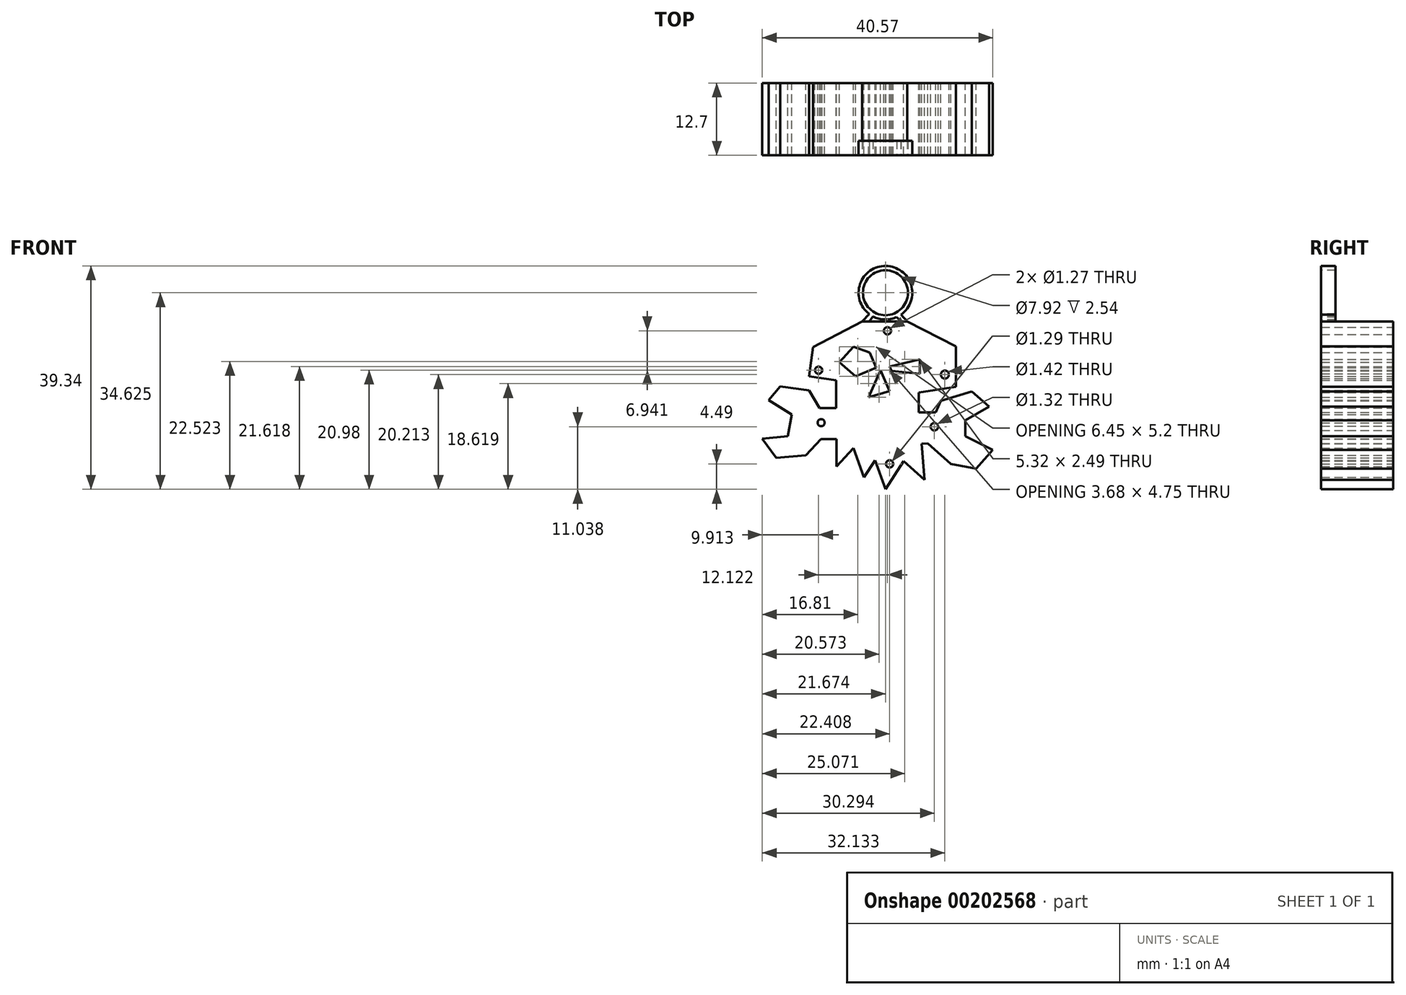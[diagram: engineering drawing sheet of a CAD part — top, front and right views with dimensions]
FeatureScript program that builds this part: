
annotation { "Feature Type Name" : "Feature", "Feature Type Description" : "" }
export const myFeature = defineFeature(function(context is Context, id is Id, definition is map)
    precondition{}
    {
        {
            var Q0;
            Q0=qCreatedBy(makeId("Front.planeOp"),FACE);
            var sketch = newSketch(context, id + "F0", { "sketchPlane" : qUnion([Q0])});
            skLineSegment(sketch, "E0", {"start": v(-63.88, 11.24) * mm, "end": v(-59.81, 8.7) * mm});
            skLineSegment(sketch, "E1", {"start": v(-59.81, 8.7) * mm, "end": v(-60.55, 4.9) * mm});
            skLineSegment(sketch, "E2", {"start": v(-60.55, 4.9) * mm, "end": v(-65.02, 4.45) * mm});
            skLineSegment(sketch, "E3", {"start": v(-65.02, 4.45) * mm, "end": v(-62.58, 1.06) * mm});
            skLineSegment(sketch, "E4", {"start": v(-62.58, 1.06) * mm, "end": v(-57.38, 1.51) * mm});
            skLineSegment(sketch, "E5", {"start": v(-57.38, 1.51) * mm, "end": v(-54.66, 4.4) * mm});
            skLineSegment(sketch, "E6", {"start": v(-54.66, 4.4) * mm, "end": v(-53.19, 4.4) * mm});
            skLineSegment(sketch, "E7", {"start": v(-53.19, 4.4) * mm, "end": v(-51.94, 4.4) * mm});
            skLineSegment(sketch, "E8", {"start": v(-51.94, 4.4) * mm, "end": v(-51.94, -0.47) * mm});
            skLineSegment(sketch, "E9", {"start": v(-51.94, -0.47) * mm, "end": v(-49, 2.81) * mm});
            skLineSegment(sketch, "E10", {"start": v(-49, 2.81) * mm, "end": v(-47.14, -2.4) * mm});
            skLineSegment(sketch, "E11", {"start": v(-47.14, -2.4) * mm, "end": v(-45.15, 0.6) * mm});
            skLineSegment(sketch, "E12", {"start": v(-45.15, 0.6) * mm, "end": v(-43.34, -4.49) * mm});
            skLineSegment(sketch, "E13", {"start": v(-43.34, -4.49) * mm, "end": v(-40.12, 0.5) * mm});
            skLineSegment(sketch, "E14", {"start": v(-40.12, 0.5) * mm, "end": v(-36.47, -2.78) * mm});
            skLineSegment(sketch, "E15", {"start": v(-36.47, -2.78) * mm, "end": v(-36.95, 3.55) * mm});
            skLineSegment(sketch, "E16", {"start": v(-36.95, 3.55) * mm, "end": v(-35.88, 3.63) * mm});
            skLineSegment(sketch, "E17", {"start": v(-35.88, 3.63) * mm, "end": v(-31.84, 0) * mm});
            skLineSegment(sketch, "E18", {"start": v(-31.84, 0) * mm, "end": v(-27.39, -0.8) * mm});
            skLineSegment(sketch, "E19", {"start": v(-27.39, -0.8) * mm, "end": v(-24.45, 2.47) * mm});
            skLineSegment(sketch, "E20", {"start": v(-24.45, 2.47) * mm, "end": v(-29.31, 4.9) * mm});
            skLineSegment(sketch, "E21", {"start": v(-29.31, 4.9) * mm, "end": v(-29.31, 7.68) * mm});
            skLineSegment(sketch, "E22", {"start": v(-29.31, 7.68) * mm, "end": v(-25.12, 10.06) * mm});
            skLineSegment(sketch, "E23", {"start": v(-25.12, 10.06) * mm, "end": v(-28.16, 12.78) * mm});
            skLineSegment(sketch, "E24", {"start": v(-28.16, 12.78) * mm, "end": v(-33.61, 11.13) * mm});
            skLineSegment(sketch, "E25", {"start": v(-33.61, 11.13) * mm, "end": v(-34.52, 9.1) * mm});
            skLineSegment(sketch, "E26", {"start": v(-34.52, 9.1) * mm, "end": v(-37.46, 9.1) * mm});
            skLineSegment(sketch, "E27", {"start": v(-37.46, 9.1) * mm, "end": v(-37.46, 12.54) * mm});
            skLineSegment(sketch, "E28", {"start": v(-37.46, 12.54) * mm, "end": v(-30.95, 13.56) * mm});
            skLineSegment(sketch, "E29", {"start": v(-30.95, 13.56) * mm, "end": v(-30.95, 20.7) * mm});
            skLineSegment(sketch, "E30", {"start": v(-30.95, 20.7) * mm, "end": v(-39.5, 25.05) * mm});
            skLineSegment(sketch, "E31", {"start": v(-39.5, 25.05) * mm, "end": v(-47.47, 25.05) * mm});
            skLineSegment(sketch, "E32", {"start": v(-47.47, 25.05) * mm, "end": v(-56.08, 20.58) * mm});
            skLineSegment(sketch, "E33", {"start": v(-56.08, 20.58) * mm, "end": v(-56.81, 15.43) * mm});
            skLineSegment(sketch, "E34", {"start": v(-56.81, 15.43) * mm, "end": v(-52.02, 14.75) * mm});
            skLineSegment(sketch, "E35", {"start": v(-52.02, 14.75) * mm, "end": v(-52.02, 9.83) * mm});
            skLineSegment(sketch, "E36", {"start": v(-52.02, 9.83) * mm, "end": v(-54.94, 9.83) * mm});
            skLineSegment(sketch, "E37", {"start": v(-54.94, 9.83) * mm, "end": v(-56.81, 12.94) * mm});
            skLineSegment(sketch, "E38", {"start": v(-56.81, 12.94) * mm, "end": v(-61.85, 13.62) * mm});
            skLineSegment(sketch, "E39", {"start": v(-61.85, 13.62) * mm, "end": v(-63.88, 11.24) * mm});
            skLineSegment(sketch, "E40", {"start": v(-51.44, 17.92) * mm, "end": v(-49, 20.63) * mm});
            skLineSegment(sketch, "E41", {"start": v(-49, 20.63) * mm, "end": v(-46.12, 19.62) * mm});
            skLineSegment(sketch, "E42", {"start": v(-46.12, 19.62) * mm, "end": v(-44.98, 16.96) * mm});
            skLineSegment(sketch, "E43", {"start": v(-44.98, 16.96) * mm, "end": v(-48.58, 15.43) * mm});
            skLineSegment(sketch, "E44", {"start": v(-48.58, 15.43) * mm, "end": v(-51.44, 17.92) * mm});
            skLineSegment(sketch, "E45", {"start": v(-42.6, 17.13) * mm, "end": v(-37.29, 18.37) * mm});
            skLineSegment(sketch, "E46", {"start": v(-37.29, 18.37) * mm, "end": v(-37.29, 15.88) * mm});
            skLineSegment(sketch, "E47", {"start": v(-37.29, 15.88) * mm, "end": v(-42.21, 16.4) * mm});
            skLineSegment(sketch, "E48", {"start": v(-42.21, 16.4) * mm, "end": v(-42.6, 17.13) * mm});
            skLineSegment(sketch, "E49", {"start": v(-46.29, 11.75) * mm, "end": v(-44.2, 16.5) * mm});
            skLineSegment(sketch, "E50", {"start": v(-44.2, 16.5) * mm, "end": v(-42.6, 12.78) * mm});
            skLineSegment(sketch, "E51", {"start": v(-42.6, 12.78) * mm, "end": v(-46.29, 11.75) * mm});
            skLineSegment(sketch, "E52", {"start": v(-53.19, 9.83) * mm, "end": v(-53.19, 4.4) * mm});
            skLineSegment(sketch, "E53", {"start": v(-35.99, 9.1) * mm, "end": v(-35.88, 3.63) * mm});
            skCircle(sketch, "E54", {"center": v(-42.99, 23.43) * mm, "radius": 0.63 * mm});
            skCircle(sketch, "E55", {"center": v(-32.89, 15.72) * mm, "radius": 0.7 * mm});
            skCircle(sketch, "E56", {"center": v(-34.73, 6.55) * mm, "radius": 0.66 * mm});
            skCircle(sketch, "E57", {"center": v(-42.61, 0) * mm, "radius": 0.64 * mm});
            skCircle(sketch, "E58", {"center": v(-54.66, 7.26) * mm, "radius": 0.63 * mm});
            skCircle(sketch, "E59", {"center": v(-55.1, 16.5) * mm, "radius": 0.63 * mm});
            skSolve(sketch);
        }
        {
            var Q0;
            Q0=makeQuery(id+"F0.imprint","IMPRINT",FACE,{"disambiguationData":[TD([[makeQuery(id+"F0.imprint","IMPRINT",EDGE,{"derivedFrom":sQuery(id+"F0.wireOp",EDGE,"E0")}),1.0]])]});
            var Q1;
            Q1=makeQuery(id+"F0.imprint","IMPRINT",FACE,{"disambiguationData":[TD([[makeQuery(id+"F0.imprint","IMPRINT",EDGE,{"derivedFrom":sQuery(id+"F0.wireOp",EDGE,"E17")}),1.0]])]});
            var Q2;
            Q2=makeQuery(id+"F0.imprint","IMPRINT",FACE,{"disambiguationData":[TD([[makeQuery(id+"F0.imprint","IMPRINT",EDGE,{"derivedFrom":sQuery(id+"F0.wireOp",EDGE,"E7")}),1.0]])]});
            extrude(context, id + "F1", {"entities" : qUnion([Q0, Q1, Q2]), "depth" : 12.7 * mm});
        }
        {
            var Q0;
            Q0=sQuery(id+"F0.wireOp",EDGE,"E59");
            var Q1;
            Q1=sQuery(id+"F0.wireOp",EDGE,"E54");
            var Q2;
            Q2=sQuery(id+"F0.wireOp",EDGE,"E55");
            var Q3;
            Q3=sQuery(id+"F0.wireOp",EDGE,"E56");
            var Q4;
            Q4=sQuery(id+"F0.wireOp",EDGE,"E57");
            var Q5;
            Q5=sQuery(id+"F0.wireOp",EDGE,"E58");
            extrude(context, id + "F2", {"bodyType" : ToolBodyType.SURFACE, "surfaceEntities" : qUnion([Q0, Q1, Q2, Q3, Q4, Q5]), "depth" : 13.46 * mm});
        }
        {
            var Q0;
            Q0=makeQuery(id+"F1.opExtrude","CAP_FACE",FACE,{"disambiguationData":[OSD([sQuery(id+"F0.wireOp",EDGE,"E0"),sQuery(id+"F0.wireOp",EDGE,"E1"),sQuery(id+"F0.wireOp",EDGE,"E2"),sQuery(id+"F0.wireOp",EDGE,"E3"),sQuery(id+"F0.wireOp",EDGE,"E4"),sQuery(id+"F0.wireOp",EDGE,"E5"),sQuery(id+"F0.wireOp",EDGE,"E6"),sQuery(id+"F0.wireOp",EDGE,"E7"),sQuery(id+"F0.wireOp",EDGE,"E8"),sQuery(id+"F0.wireOp",EDGE,"E9"),sQuery(id+"F0.wireOp",EDGE,"E10"),sQuery(id+"F0.wireOp",EDGE,"E11"),sQuery(id+"F0.wireOp",EDGE,"E12"),sQuery(id+"F0.wireOp",EDGE,"E13"),sQuery(id+"F0.wireOp",EDGE,"E14"),sQuery(id+"F0.wireOp",EDGE,"E15"),sQuery(id+"F0.wireOp",EDGE,"E16"),sQuery(id+"F0.wireOp",EDGE,"E17"),sQuery(id+"F0.wireOp",EDGE,"E18"),sQuery(id+"F0.wireOp",EDGE,"E19"),sQuery(id+"F0.wireOp",EDGE,"E20"),sQuery(id+"F0.wireOp",EDGE,"E21"),sQuery(id+"F0.wireOp",EDGE,"E22"),sQuery(id+"F0.wireOp",EDGE,"E23"),sQuery(id+"F0.wireOp",EDGE,"E24"),sQuery(id+"F0.wireOp",EDGE,"E25"),sQuery(id+"F0.wireOp",EDGE,"E26"),sQuery(id+"F0.wireOp",EDGE,"E27"),sQuery(id+"F0.wireOp",EDGE,"E28"),sQuery(id+"F0.wireOp",EDGE,"E29"),sQuery(id+"F0.wireOp",EDGE,"E30"),sQuery(id+"F0.wireOp",EDGE,"E31"),sQuery(id+"F0.wireOp",EDGE,"E32"),sQuery(id+"F0.wireOp",EDGE,"E33"),sQuery(id+"F0.wireOp",EDGE,"E34"),sQuery(id+"F0.wireOp",EDGE,"E35"),sQuery(id+"F0.wireOp",EDGE,"E36"),sQuery(id+"F0.wireOp",EDGE,"E37"),sQuery(id+"F0.wireOp",EDGE,"E38"),sQuery(id+"F0.wireOp",EDGE,"E39"),sQuery(id+"F0.wireOp",EDGE,"E40"),sQuery(id+"F0.wireOp",EDGE,"E41"),sQuery(id+"F0.wireOp",EDGE,"E42"),sQuery(id+"F0.wireOp",EDGE,"E43"),sQuery(id+"F0.wireOp",EDGE,"E44"),sQuery(id+"F0.wireOp",EDGE,"E45"),sQuery(id+"F0.wireOp",EDGE,"E46"),sQuery(id+"F0.wireOp",EDGE,"E47"),sQuery(id+"F0.wireOp",EDGE,"E48"),sQuery(id+"F0.wireOp",EDGE,"E49"),sQuery(id+"F0.wireOp",EDGE,"E50"),sQuery(id+"F0.wireOp",EDGE,"E51"),sQuery(id+"F0.wireOp",EDGE,"E54"),sQuery(id+"F0.wireOp",EDGE,"E55"),sQuery(id+"F0.wireOp",EDGE,"E56"),sQuery(id+"F0.wireOp",EDGE,"E57"),sQuery(id+"F0.wireOp",EDGE,"E58"),sQuery(id+"F0.wireOp",EDGE,"E59")])],"isStart":false});
            var sketch = newSketch(context, id + "F3", { "sketchPlane" : qUnion([Q0])});
            skLineSegment(sketch, "E60", {"start": v(-47.47, 25.05) * mm, "end": v(-46.21, 26.38) * mm});
            skLineSegment(sketch, "E61", {"start": v(-39.5, 25.05) * mm, "end": v(-40.67, 26.38) * mm});
            skLineSegment(sketch, "E62", {"start": v(-40.67, 25.05) * mm, "end": v(-41.85, 26.38) * mm});
            skLineSegment(sketch, "E63", {"start": v(-46.21, 25.05) * mm, "end": v(-45.18, 26.38) * mm});
            skCircle(sketch, "E64", {"center": v(-43.35, 30.13) * mm, "radius": 4.72 * mm});
            skCircle(sketch, "E65", {"center": v(-43.35, 30.13) * mm, "radius": 3.96 * mm});
            skSolve(sketch);
        }
        {
            var Q0;
            Q0 = qSketchRegion(id + "F3", true);
            var Q1;
            {var subQ0=sQuery(id+"F3.wireOp",EDGE,"E60");Q1=makeQuery(id+"F3.imprint","IMPRINT",FACE,{"disambiguationData":[TD([[makeQuery(id+"F3.imprint","IMPRINT",EDGE,{"derivedFrom":subQ0}),-1.0]])]});}
            var Q2;
            {var subQ1=makeQuery(id+"F1.opExtrude","CAP_EDGE",EDGE,{"disambiguationData":[OSD([sQuery(id+"F0.wireOp",EDGE,"E31")])],"isStart":false});var subQ5=sQuery(id+"F3.wireOp",EDGE,"E62");var subQ6=makeQuery(id+"F3.imprint","INTERSECT",VERTEX,{"derivedFrom":[subQ1,subQ5]});Q2=makeQuery(id+"F3.imprint","IMPRINT",FACE,{"disambiguationData":[TD([[makeQuery(id+"F3.imprint","IMPRINT",EDGE,{"disambiguationData":[TD([[subQ6,-1.0]])],"derivedFrom":subQ5}),-1.0]])]});}
            extrude(context, id + "F4", {"entities" : qUnion([Q0, Q1, Q2]), "oppositeDirection" : true, "depth" : 2.54 * mm});
        }
    });
